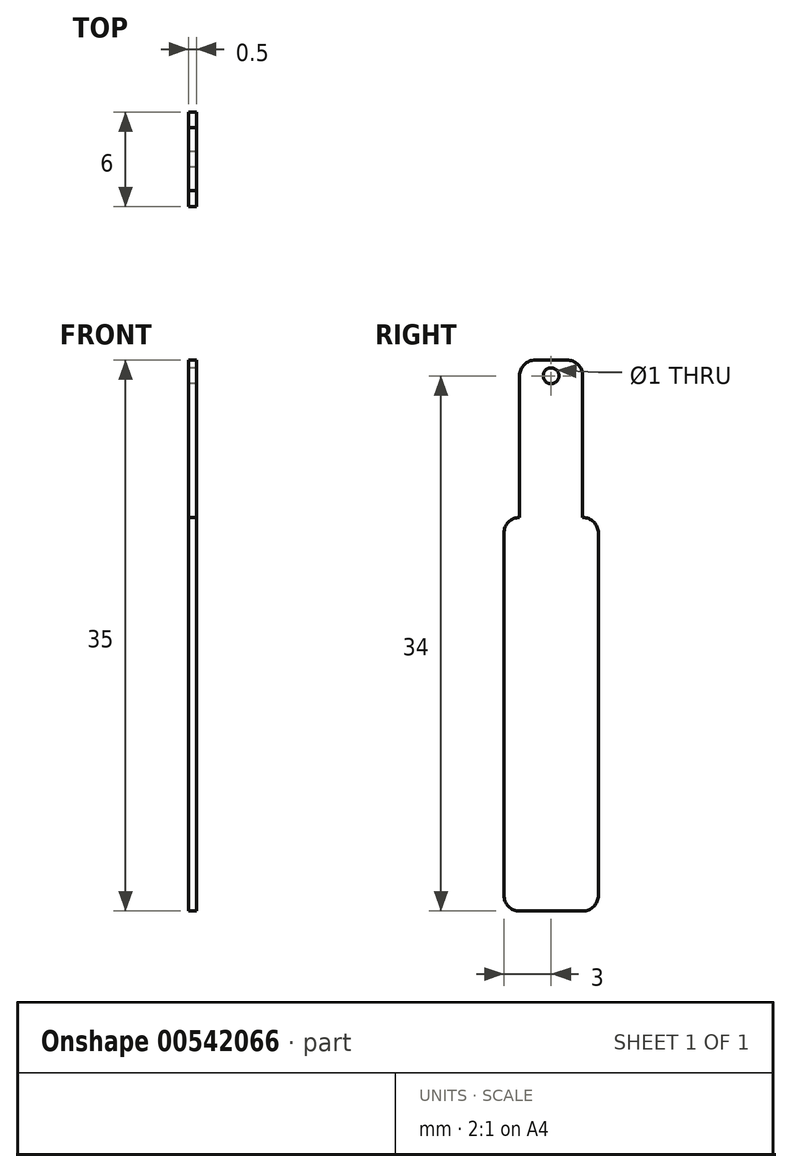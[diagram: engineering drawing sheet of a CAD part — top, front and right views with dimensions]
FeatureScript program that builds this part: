
annotation { "Feature Type Name" : "Feature", "Feature Type Description" : "" }
export const myFeature = defineFeature(function(context is Context, id is Id, definition is map)
    precondition{}
    {
        {
            var Q0;
            Q0=qCreatedBy(makeId("Right.planeOp"),FACE);
            var sketch = newSketch(context, id + "F0", { "sketchPlane" : qUnion([Q0])});
            skLineSegment(sketch, "E0.bottom", {"start": v(-2, -3) * mm, "end": v(2, -3) * mm});
            skLineSegment(sketch, "E0.left", {"start": v(-3, -2) * mm, "end": v(-3, 21) * mm});
            skLineSegment(sketch, "E0.right", {"start": v(3, -2) * mm, "end": v(3, 21) * mm});
            skPoint(sketch, "E1.visualSharp", {"position": v(-3, 22) * mm});
            skArc(sketch, "E1.filletArc", {"start": v(-2, 22) * mm, "mid": v(-2.7, 21.7) * mm, "end": v(-3, 21) * mm});
            skPoint(sketch, "E2.visualSharp", {"position": v(3, 22) * mm});
            skArc(sketch, "E2.filletArc", {"start": v(3, 21) * mm, "mid": v(2.7, 21.7) * mm, "end": v(2, 22) * mm});
            skPoint(sketch, "E3.visualSharp", {"position": v(3, -3) * mm});
            skArc(sketch, "E3.filletArc", {"start": v(2, -3) * mm, "mid": v(2.7, -2.7) * mm, "end": v(3, -2) * mm});
            skPoint(sketch, "E4.visualSharp", {"position": v(-3, -3) * mm});
            skArc(sketch, "E4.filletArc", {"start": v(-3, -2) * mm, "mid": v(-2.7, -2.7) * mm, "end": v(-2, -3) * mm});
            skLineSegment(sketch, "E5", {"start": v(-2, 22) * mm, "end": v(-2, 31) * mm});
            skLineSegment(sketch, "E6", {"start": v(-1, 32) * mm, "end": v(1, 32) * mm});
            skLineSegment(sketch, "E7", {"start": v(2, 22) * mm, "end": v(2, 31) * mm});
            skPoint(sketch, "E8.visualSharp", {"position": v(-2, 32) * mm});
            skArc(sketch, "E8.filletArc", {"start": v(-1, 32) * mm, "mid": v(-1.7, 31.7) * mm, "end": v(-2, 31) * mm});
            skPoint(sketch, "E9.visualSharp", {"position": v(2, 32) * mm});
            skArc(sketch, "E9.filletArc", {"start": v(2, 31) * mm, "mid": v(1.7, 31.7) * mm, "end": v(1, 32) * mm});
            skCircle(sketch, "E10", {"center": v(0, 31) * mm, "radius": 0.5 * mm});
            skSolve(sketch);
        }
        {
            var Q0;
            Q0 = qSketchRegion(id + "F0", true);
            extrude(context, id + "F1", {"entities" : qUnion([Q0]), "depth" : .5 * mm, "offsetDistance" : 25 * mm});
        }
    });
